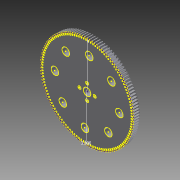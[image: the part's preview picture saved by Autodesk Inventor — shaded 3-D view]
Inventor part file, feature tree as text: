
AUTODESK INVENTOR PART (.ipt)
format: ipt  version: 2015 (Build 190159000, 159)  size: 1,122,816 bytes
history: native  units: in
note: dims shown in document units (in); Inventor stores cm internally (conversion verified against a paired STEP export)
features: sketch x3, extrude x2, pattern_circular x1, projected_geometry x1
ambient origin geometry x8: Origin, YZ Plane, XZ Plane, XY Plane, X Axis, Y Axis, Z Axis, Center Point
bodies: Solid1 (feature_tree)
feature tree (7):
  extrude  "Extrusion1"  Depth=0.3125in
  extrude  "Extrusion2"  Depth=0.3125in
  pattern_circular  "Circular Pattern1"  Count=4 Angle=360.0deg
  sketch  "Sketch3"  dims[d8=0.3125in d9=0.875in d10=1.0in d11=3.1496in d13=360.0deg d15=0.25in d16=0.0in d17=0.0156in d18=0.0625in d19=0.0156in d20=0.0417in d21=0.25in d22=0.0in d23=47.2441in d24=360.0deg d27=3.8in]
  sketch  "Sketch1"  dims[d0=3.625in d1=0.3125in]
  sketch  "Sketch2"  dims[d2=0.125in d3=0.3125in d4=1.5748in d6=360.0deg]
  projected_geometry  "Projected Loop1"
